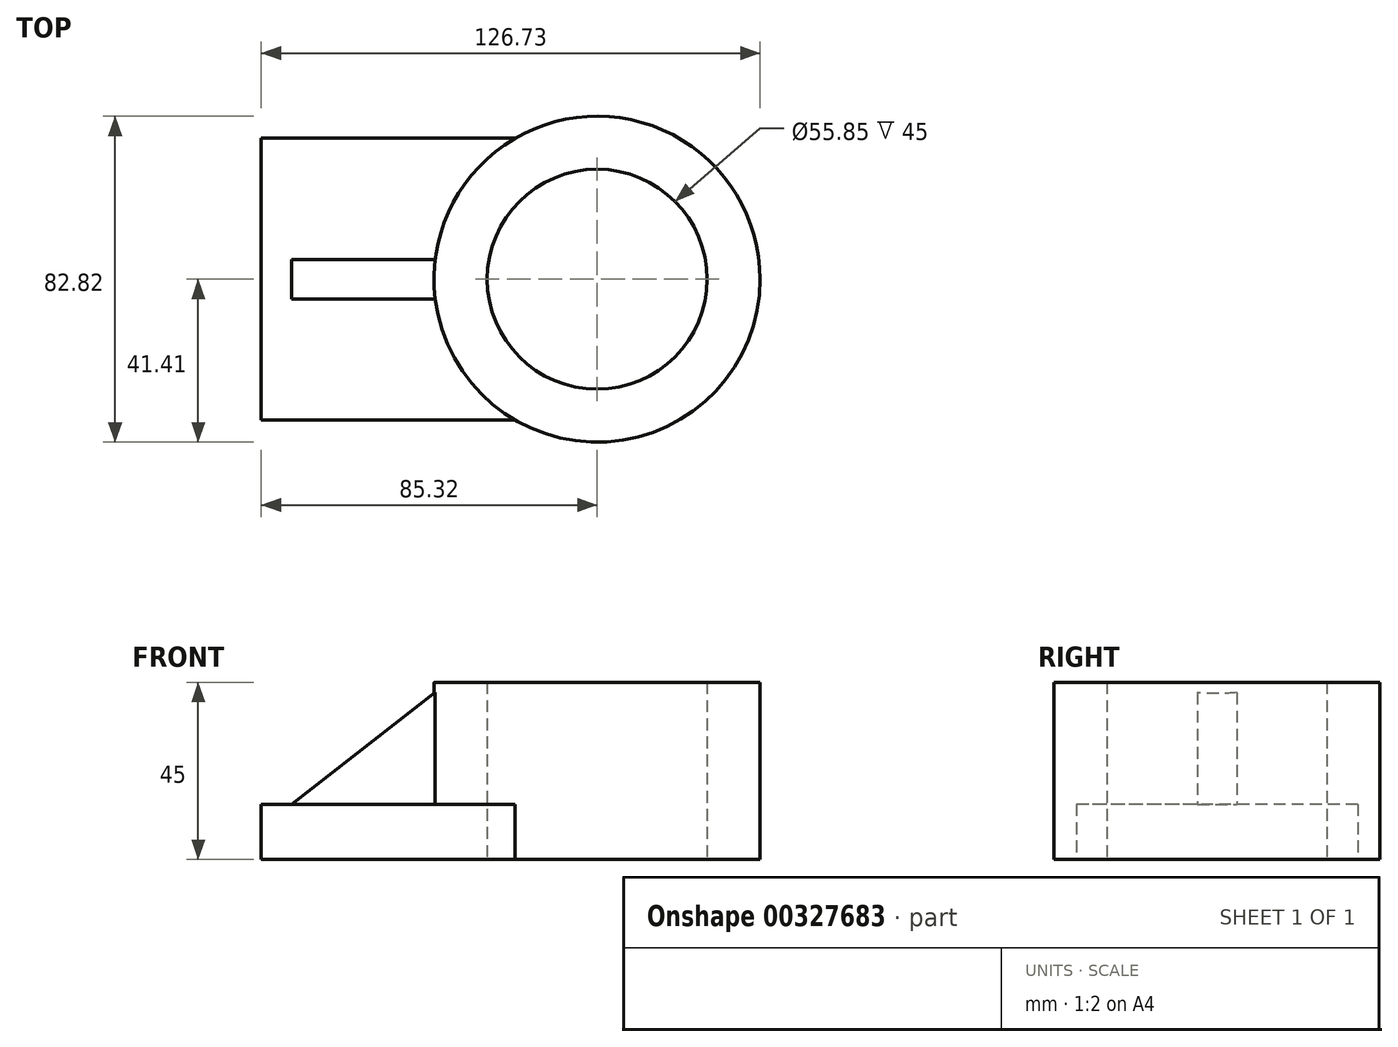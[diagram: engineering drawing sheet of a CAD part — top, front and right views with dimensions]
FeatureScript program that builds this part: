
annotation { "Feature Type Name" : "Feature", "Feature Type Description" : "" }
export const myFeature = defineFeature(function(context is Context, id is Id, definition is map)
    precondition{}
    {
        {
            var Q0;
            Q0=qCreatedBy(makeId("Top.planeOp"),FACE);
            var sketch = newSketch(context, id + "F0", { "sketchPlane" : qUnion([Q0])});
            skCircle(sketch, "E0", {"center": v(32.4, 0) * mm, "radius": 27.92 * mm});
            skCircle(sketch, "E1", {"center": v(32.4, 0) * mm, "radius": 41.41 * mm});
            skSolve(sketch);
        }
        {
            var Q0;
            Q0 = qSketchRegion(id + "F0", true);
            extrude(context, id + "F1", {"entities" : qUnion([Q0]), "depth" : 45 * mm});
        }
        {
            var Q0;
            Q0=makeQuery(id+"F1.opExtrude","CAP_FACE",FACE,{"disambiguationData":[OSD([sQuery(id+"F0.wireOp",EDGE,"E0"),sQuery(id+"F0.wireOp",EDGE,"E1")])],"isStart":true});
            var sketch = newSketch(context, id + "F2", { "sketchPlane" : qUnion([Q0])});
            skLineSegment(sketch, "E2.bottom", {"start": v(11.56, -35.78) * mm, "end": v(-52.9, -35.78) * mm});
            skLineSegment(sketch, "E2.top", {"start": v(11.56, 35.78) * mm, "end": v(-52.9, 35.78) * mm});
            skLineSegment(sketch, "E2.right", {"start": v(-52.9, -35.78) * mm, "end": v(-52.9, 35.78) * mm});
            skPoint(sketch, "E2.middle", {"position": v(-20.68, 0) * mm});
            skArc(sketch, "E3.0", {"start": v(11.56, 35.78) * mm, "mid": v(-9, 0) * mm, "end": v(11.56, -35.78) * mm});
            skSolve(sketch);
        }
        {
            var Q0;
            Q0 = qSketchRegion(id + "F2", true);
            extrude(context, id + "F3", {"entities" : qUnion([Q0]), "operationType" : NewBodyOperationType.ADD, "oppositeDirection" : true, "depth" : 14 * mm});
        }
        {
            var Q0;
            Q0=qCreatedBy(makeId("Front.planeOp"),FACE);
            var sketch = newSketch(context, id + "F4", { "sketchPlane" : qUnion([Q0])});
            skLineSegment(sketch, "E4", {"start": v(-47.7, 12.1) * mm, "end": v(-6.9, 43.75) * mm});
            skLineSegment(sketch, "E5", {"start": v(-6.9, 43.75) * mm, "end": v(-6.9, 12.1) * mm});
            skLineSegment(sketch, "E6", {"start": v(-6.9, 12.1) * mm, "end": v(-47.7, 12.1) * mm});
            skSolve(sketch);
        }
        {
            var Q0;
            Q0 = qSketchRegion(id + "F4", true);
            extrude(context, id + "F5", {"entities" : qUnion([Q0]), "operationType" : NewBodyOperationType.ADD, "endBound" : BoundingType.SYMMETRIC, "depth" : 10 * mm});
        }
    });
